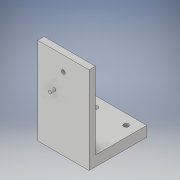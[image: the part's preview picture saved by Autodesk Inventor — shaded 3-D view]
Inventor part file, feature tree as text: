
AUTODESK INVENTOR PART (.ipt)
format: ipt  version: 2017 (Build 210142000, 142)  size: 148,992 bytes
history: native  units: in
note: dims shown in document units (in); Inventor stores cm internally (conversion verified against a paired STEP export)
features: extrude x6, sketch x6
ambient origin geometry x8: Origin, YZ Plane, XZ Plane, XY Plane, X Axis, Y Axis, Z Axis, Center Point
bodies: Solid1 (feature_tree)
feature tree (12):
  extrude  "Extrusion1"  Depth=0.15in
  extrude  "Extrusion2"  Depth=0.15in
  extrude  "Extrusion3"  Depth=0.25in TaperAngle=0.0deg
  extrude  "Extrusion4"  Depth=2.0in TaperAngle=0.0deg
  extrude  "Extrusion5"  Depth=0.4in
  extrude  "Extrusion6"  Depth=0.4in
  sketch  "Sketch1"  dims[d0=0.75in d1=0.75in d2=0.35in d3=0.15in]
  sketch  "Sketch2"  dims[d4=0.15in d5=0.15in]
  sketch  "Sketch3"  dims[d6=0.25in d7=0.0in d8=0.25in d9=0.0in]
  sketch  "Sketch4"  dims[d10=0.4in d11=2.0in d12=0.0in]
  sketch  "Sketch5"  dims[d13=0.1875in d14=0.1875in d17=0.4in]
  sketch  "Sketch6"  dims[d18=0.4in d19=0.4in d20=0.4in d21=2.0in d22=0.0in d23=0.25in d24=0.25in d25=0.0in d26=0.0in d27=0.12in d28=0.3162in d29=0.31in d30=0.175in d31=0.0in d32=2.826in d33=1.7434in d34=1.0in d35=0.0in d36=0.0in d37=3.396in]
